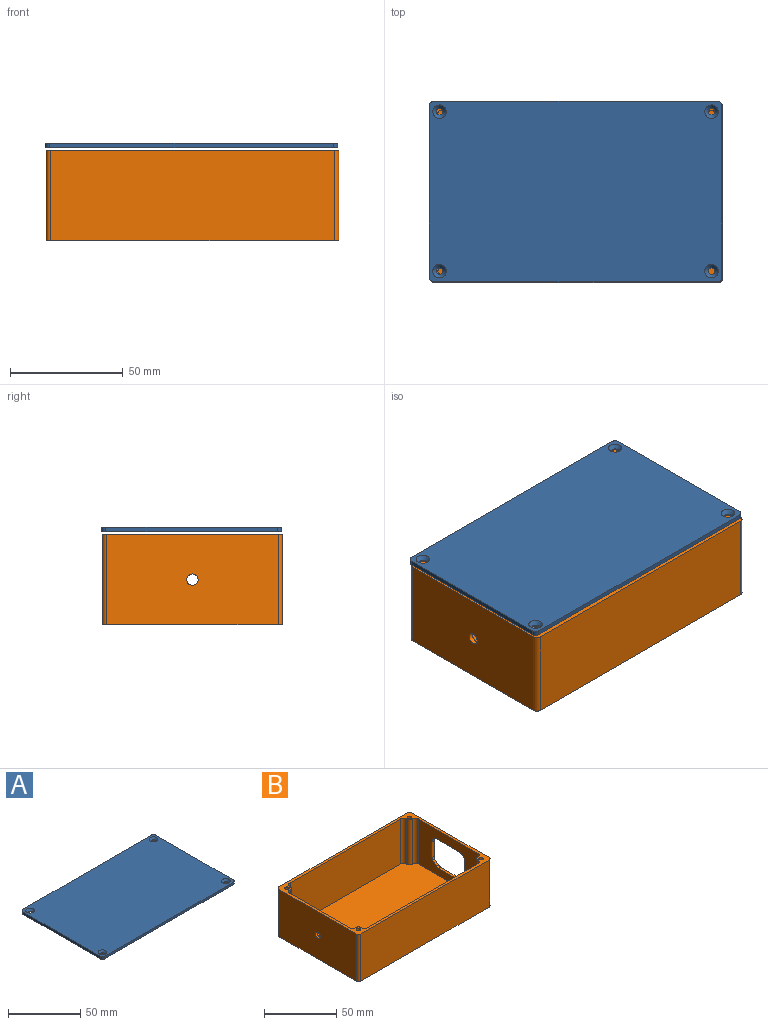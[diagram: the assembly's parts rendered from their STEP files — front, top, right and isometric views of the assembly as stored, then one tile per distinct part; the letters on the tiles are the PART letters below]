
ASSEMBLY  parts=2 mates=1
PART A: 18 faces, bbox 130x80x2 mm
  f0: plane 126x2mm, normal (0,1,0), area 252mm2, adj f8,f9,f10,f13
  f1: plane 76x2mm, normal (-1,0,0), area 152mm2, adj f8,f9,f10,f11
  f2: plane 126x2mm, normal (0,-1,0), area 252mm2, adj f8,f9,f11,f12
  f3: cylinder r=1.5mm len=3mm, axis (0,0,-1), area 4.7mm2, adj f9,f16
  f4: cylinder r=1.5mm len=3mm, axis (0,0,-1), area 4.7mm2, adj f9,f14
  f5: cylinder r=1.5mm len=3mm, axis (0,0,-1), area 4.7mm2, adj f9,f17
  f6: cylinder r=1.5mm len=3mm, axis (0,0,-1), area 4.7mm2, adj f9,f15
  f7: plane 76x2mm, normal (1,0,0), area 152mm2, adj f8,f9,f12,f13
  f8: plane 130x80mm, normal (0,0,1), area 10283.5mm2, adj f0,f1,f2,f7,f10,f11,f12,f13
  f9: plane 130x80mm, normal (0,0,-1), area 10368.3mm2, adj f0,f1,f2,f3,f4,f5,f6,f7
  f10: cylinder r=2mm len=2mm, axis (0,0,1), area 6.3mm2, adj f0,f1,f8,f9
  f11: cylinder r=2mm len=2mm, axis (0,0,-1), area 6.3mm2, adj f1,f2,f8,f9
  f12: cylinder r=2mm len=2mm, axis (0,0,1), area 6.3mm2, adj f2,f7,f8,f9
  f13: cylinder r=2mm len=2mm, axis (0,0,-1), area 6.3mm2, adj f0,f7,f8,f9
  f14: cone r=1.5mm half-angle=45deg, axis (0,0,1), area 30mm2, adj f4,f8
  f15: cone r=1.5mm half-angle=45deg, axis (0,0,1), area 30mm2, adj f6,f8
  f16: cone r=1.5mm half-angle=45deg, axis (0,0,1), area 30mm2, adj f3,f8
  f17: cone r=1.5mm half-angle=45deg, axis (0,0,1), area 30mm2, adj f5,f8
PART B: 48 faces, bbox 130x80x40 mm
  f0: plane 58x38mm, normal (-1,0,0), area 1472.5mm2, adj f2,f6,f19,f20,f21,f22,f23,f24
  f1: plane 76x40mm, normal (1,0,0), area 2308.5mm2, adj f6,f10,f19,f20,f21,f22,f23,f24
  f2: plane 126x76mm, normal (0,0,1), area 9424.3mm2, adj f0,f3,f4,f5,f36,f37,f38,f39
  f3: plane 58x38mm, normal (1,0,0), area 2184.4mm2, adj f2,f6,f31,f37,f45
  f4: plane 108x38mm, normal (0,1,0), area 4104mm2, adj f2,f6,f36,f41
  f5: plane 108x38mm, normal (0,-1,0), area 4104mm2, adj f2,f6,f42,f47
  f6: plane 130x80mm, normal (0,0,1), area 944mm2, adj f0,f1,f3,f4,f5,f7,f8,f9
  f7: plane 126x40mm, normal (0,1,0), area 5040mm2, adj f6,f10,f32,f35
  f8: plane 76x40mm, normal (-1,0,0), area 3020.4mm2, adj f6,f10,f31,f32,f33
  f9: plane 126x40mm, normal (0,-1,0), area 5040mm2, adj f6,f10,f33,f34
  f10: plane 130x80mm, normal (0,0,-1), area 10396.6mm2, adj f1,f7,f8,f9,f32,f33,f34,f35
  f11: cylinder r=1.5mm len=20mm, axis (0,0,1), area 188.5mm2, adj f6,f12
  f12: plane 3x3mm, normal (0,0,1), area 7.1mm2, adj f11
  f13: cylinder r=1.5mm len=20mm, axis (0,0,1), area 188.5mm2, adj f6,f14
  f14: plane 3x3mm, normal (0,0,1), area 7.1mm2, adj f13
  f15: cylinder r=1.5mm len=20mm, axis (0,0,1), area 188.5mm2, adj f6,f16
  f16: plane 3x3mm, normal (0,0,1), area 7.1mm2, adj f15
  f17: cylinder r=1.5mm len=20mm, axis (0,0,1), area 188.5mm2, adj f6,f18
  f18: plane 3x3mm, normal (0,0,1), area 7.1mm2, adj f17
  f19: plane 19.51x2mm, normal (0,0,1), area 39mm2, adj f0,f1,f29,f30
  f20: plane 12.76x2mm, normal (0,-1,0), area 25.5mm2, adj f0,f1,f23,f27
  f21: plane 22x2mm, normal (0,0,-1), area 44mm2, adj f0,f1,f23,f24
  f22: plane 12.76x2mm, normal (0,1,0), area 25.5mm2, adj f0,f1,f24,f28
  f23: cylinder r=5mm len=5mm, axis (-1,0,0), area 15.7mm2, adj f0,f1,f20,f21
  f24: cylinder r=5mm len=5mm, axis (1,0,0), area 15.7mm2, adj f0,f1,f21,f22
  f25: plane 3.24x3.24mm, normal (0,0.71,0.71), area 9.2mm2, adj f0,f1,f28,f29
  f26: plane 3.24x3.24mm, normal (0,-0.71,0.71), area 9.2mm2, adj f0,f1,f27,f30
  f27: cylinder r=3mm len=2.12mm, axis (-1,0,0), area 4.7mm2, adj f0,f1,f20,f26
  f28: cylinder r=3mm len=2.12mm, axis (1,0,0), area 4.7mm2, adj f0,f1,f22,f25
  f29: cylinder r=3mm len=2.12mm, axis (-1,0,0), area 4.7mm2, adj f0,f1,f19,f25
  f30: cylinder r=3mm len=2.12mm, axis (-1,0,0), area 4.7mm2, adj f0,f1,f19,f26
  f31: cylinder r=2.5mm len=5mm, axis (-1,0,0), area 31.4mm2, adj f3,f8
  f32: cylinder r=2mm len=40mm, axis (0,0,1), area 125.7mm2, adj f6,f7,f8,f10
  f33: cylinder r=2mm len=40mm, axis (0,0,-1), area 125.7mm2, adj f6,f8,f9,f10
  f34: cylinder r=2mm len=40mm, axis (0,0,1), area 125.7mm2, adj f1,f6,f9,f10
  f35: cylinder r=2mm len=40mm, axis (0,0,-1), area 125.7mm2, adj f1,f6,f7,f10
  f36: cylinder r=3mm len=38mm, axis (0,0,-1), area 179.1mm2, adj f2,f4,f6,f38
  f37: cylinder r=3mm len=38mm, axis (0,0,1), area 179.1mm2, adj f2,f3,f6,f38
  f38: cylinder r=3mm len=38mm, axis (0,0,1), area 179.1mm2, adj f2,f6,f36,f37
  f39: cylinder r=3mm len=38mm, axis (0,0,1), area 179.1mm2, adj f0,f2,f6,f40
  f40: cylinder r=3mm len=38mm, axis (0,0,1), area 179.1mm2, adj f2,f6,f39,f41
  f41: cylinder r=3mm len=38mm, axis (0,0,1), area 179.1mm2, adj f2,f4,f6,f40
  f42: cylinder r=3mm len=38mm, axis (0,0,1), area 179.1mm2, adj f2,f5,f6,f43
  f43: cylinder r=3mm len=38mm, axis (0,0,1), area 179.1mm2, adj f2,f6,f42,f44
  f44: cylinder r=3mm len=38mm, axis (0,0,-1), area 179.1mm2, adj f0,f2,f6,f43
  f45: cylinder r=3mm len=38mm, axis (0,0,-1), area 179.1mm2, adj f2,f3,f6,f46
  f46: cylinder r=3mm len=38mm, axis (0,0,1), area 179.1mm2, adj f2,f6,f45,f47
  f47: cylinder r=3mm len=38mm, axis (0,0,-1), area 179.1mm2, adj f2,f5,f6,f46
PLACE A t=(-172.16,-2.02,68.94)mm
PLACE B t=(-33,1.07,27.72)mm fixed
MATE slider B.f15 <-> A.f6  axis (0,0,1) through (2.45,7.34,67.72)mm
